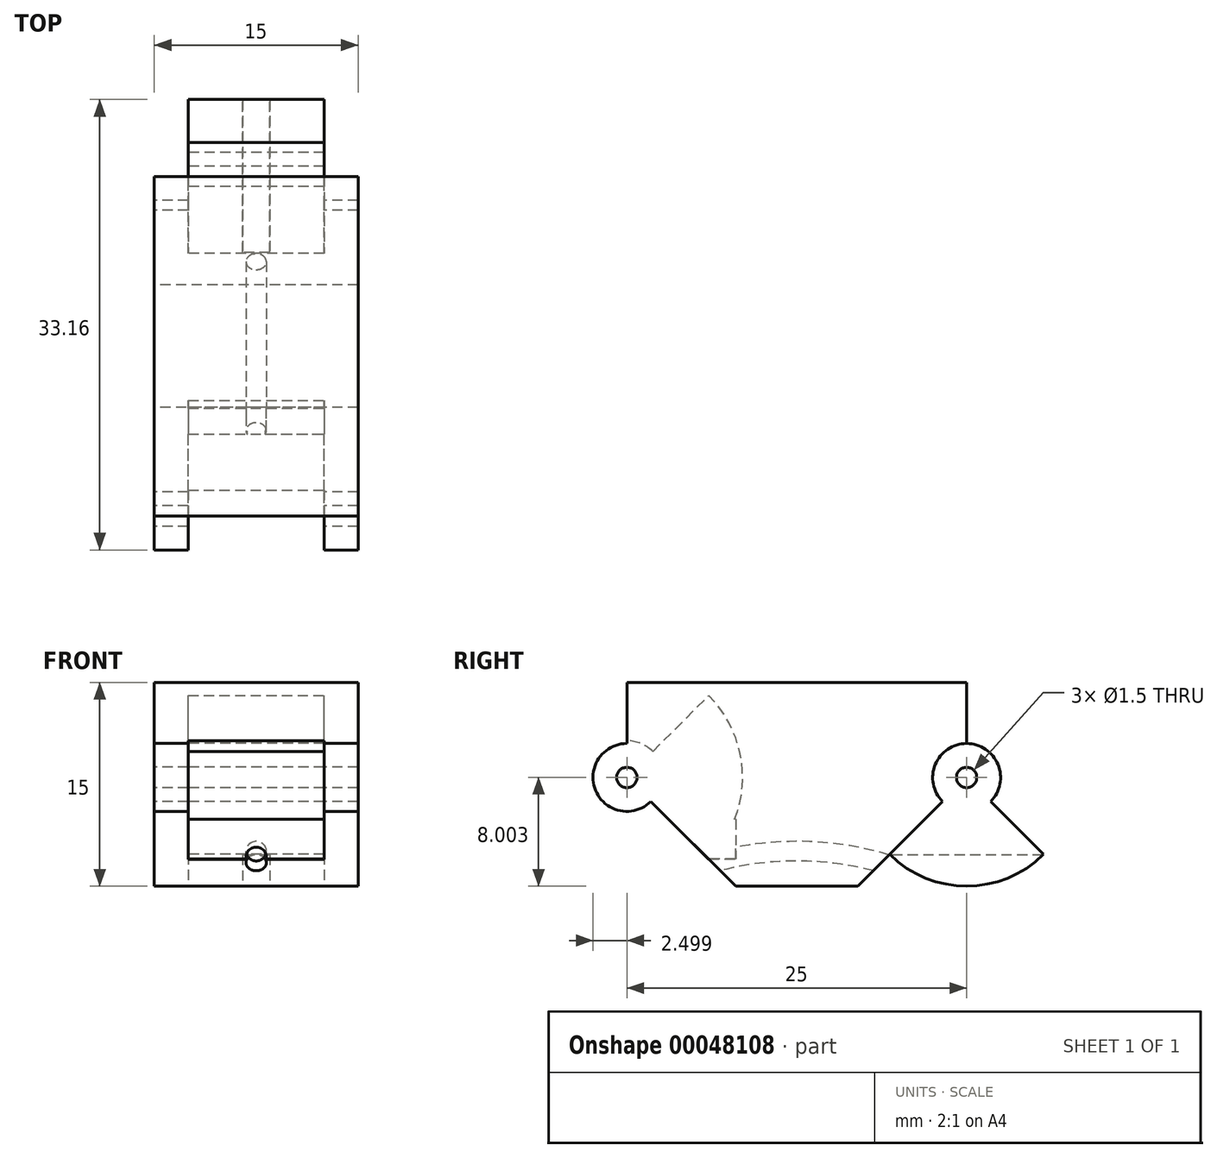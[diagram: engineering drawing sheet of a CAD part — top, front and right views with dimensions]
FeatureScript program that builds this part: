
annotation { "Feature Type Name" : "Feature", "Feature Type Description" : "" }
export const myFeature = defineFeature(function(context is Context, id is Id, definition is map)
    precondition{}
    {
        {
            var Q0;
            Q0=qCreatedBy(makeId("Right.planeOp"),FACE);
            var sketch = newSketch(context, id + "F0", { "sketchPlane" : qUnion([Q0])});
            skLineSegment(sketch, "E0.bottom", {"start": v(-39.16, 7.74) * mm, "end": v(-14.16, 7.74) * mm});
            skLineSegment(sketch, "E0.top", {"start": v(-39.16, -7.26) * mm, "end": v(-14.16, -7.26) * mm});
            skLineSegment(sketch, "E0.left", {"start": v(-39.16, 7.74) * mm, "end": v(-39.16, -7.26) * mm});
            skLineSegment(sketch, "E0.right", {"start": v(-14.16, 7.74) * mm, "end": v(-14.16, -7.26) * mm});
            skCircle(sketch, "E1", {"center": v(-14.16, 0.74) * mm, "radius": 2.5 * mm});
            skCircle(sketch, "E2", {"center": v(-14.16, 0.74) * mm, "radius": 8 * mm});
            skLineSegment(sketch, "E3", {"start": v(-14.16, 0.74) * mm, "end": v(-8.5, -4.91) * mm});
            skCircle(sketch, "E4", {"center": v(-14.16, 0.74) * mm, "radius": 0.75 * mm});
            skLineSegment(sketch, "E5", {"start": v(-14.16, 0.74) * mm, "end": v(-22.16, -7.26) * mm});
            skCircle(sketch, "E6", {"center": v(-39.16, 0.74) * mm, "radius": 2.5 * mm});
            skCircle(sketch, "E7", {"center": v(-39.16, 0.74) * mm, "radius": 0.75 * mm});
            skLineSegment(sketch, "E8", {"start": v(-39.16, 0.74) * mm, "end": v(-31.16, -7.26) * mm});
            skArc(sketch, "E9", {"start": v(-33.14, -5.28) * mm, "mid": v(-30.65, 0.74) * mm, "end": v(-33.14, 6.76) * mm});
            skLineSegment(sketch, "E10", {"start": v(-39.16, 0.74) * mm, "end": v(-32.16, 7.74) * mm});
            skSolve(sketch);
        }
        {
            var Q0;
            {var subQ3=sQuery(id+"F0.wireOp",EDGE,"E0.right");var subQ7=sQuery(id+"F0.wireOp",EDGE,"E0.bottom");var subQ8=makeQuery(id+"F0.imprint","INTERSECT",VERTEX,{"derivedFrom":[subQ7,subQ3]});Q0=makeQuery(id+"F0.imprint","IMPRINT",FACE,{"disambiguationData":[TD([[makeQuery(id+"F0.imprint","IMPRINT",EDGE,{"disambiguationData":[TD([[subQ8,1.0]])],"derivedFrom":subQ7}),-1.0]])]});}
            var Q1;
            {var subQ5=sQuery(id+"F0.wireOp",EDGE,"E0.left");var subQ11=sQuery(id+"F0.wireOp",EDGE,"E0.bottom");var subQ13=makeQuery(id+"F0.imprint","INTERSECT",VERTEX,{"derivedFrom":[subQ11,subQ5]});Q1=makeQuery(id+"F0.imprint","IMPRINT",FACE,{"disambiguationData":[TD([[makeQuery(id+"F0.imprint","IMPRINT",EDGE,{"disambiguationData":[TD([[subQ13,-1.0]])],"derivedFrom":subQ11}),-1.0]])]});}
            var Q2;
            {var subQ3=sQuery(id+"F0.wireOp",EDGE,"E6");var subQ5=sQuery(id+"F0.wireOp",EDGE,"E0.left");var subQ6=makeQuery(id+"F0.imprint","INTERSECT",VERTEX,{"disambiguationData":[OD(1.0)],"derivedFrom":[subQ5,subQ3]});Q2=makeQuery(id+"F0.imprint","IMPRINT",FACE,{"disambiguationData":[TD([[makeQuery(id+"F0.imprint","IMPRINT",EDGE,{"disambiguationData":[TD([[subQ6,1.0]])],"derivedFrom":subQ5}),1.0]])]});}
            var Q3;
            {var subQ1=sQuery(id+"F0.wireOp",EDGE,"E0.left");var subQ4=sQuery(id+"F0.wireOp",EDGE,"E6");var subQ6=makeQuery(id+"F0.imprint","INTERSECT",VERTEX,{"disambiguationData":[OD(0.0)],"derivedFrom":[subQ1,subQ4]});Q3=makeQuery(id+"F0.imprint","IMPRINT",FACE,{"disambiguationData":[TD([[makeQuery(id+"F0.imprint","IMPRINT",EDGE,{"disambiguationData":[TD([[subQ6,-1.0]])],"derivedFrom":subQ1}),-1.0]])]});}
            var Q4;
            {var subQ3=sQuery(id+"F0.wireOp",EDGE,"E6");var subQ5=sQuery(id+"F0.wireOp",EDGE,"E0.left");var subQ7=makeQuery(id+"F0.imprint","INTERSECT",VERTEX,{"disambiguationData":[OD(0.0)],"derivedFrom":[subQ5,subQ3]});Q4=makeQuery(id+"F0.imprint","IMPRINT",FACE,{"disambiguationData":[TD([[makeQuery(id+"F0.imprint","IMPRINT",EDGE,{"disambiguationData":[TD([[subQ7,-1.0]])],"derivedFrom":subQ5}),1.0]])]});}
            var Q5;
            {var subQ0=sQuery(id+"F0.wireOp",EDGE,"E9");Q5=makeQuery(id+"F0.imprint","IMPRINT",FACE,{"disambiguationData":[TD([[makeQuery(id+"F0.imprint","IMPRINT",EDGE,{"derivedFrom":subQ0}),-1.0]])]});}
            var Q6;
            {var subQ3=sQuery(id+"F0.wireOp",EDGE,"E9");Q6=makeQuery(id+"F0.imprint","IMPRINT",FACE,{"disambiguationData":[TD([[makeQuery(id+"F0.imprint","IMPRINT",EDGE,{"derivedFrom":subQ3}),1.0]])]});}
            var Q7;
            {var subQ0=sQuery(id+"F0.wireOp",EDGE,"E10");var subQ3=sQuery(id+"F0.wireOp",EDGE,"E6");var subQ4=makeQuery(id+"F0.imprint","INTERSECT",VERTEX,{"derivedFrom":[subQ3,subQ0]});Q7=makeQuery(id+"F0.imprint","IMPRINT",FACE,{"disambiguationData":[TD([[makeQuery(id+"F0.imprint","IMPRINT",EDGE,{"disambiguationData":[TD([[subQ4,1.0]])],"derivedFrom":subQ3}),1.0]])]});}
            extrude(context, id + "F1", {"entities" : qUnion([Q0, Q1, Q2, Q3, Q4, Q5, Q6, Q7]), "depth" : 15 * mm, "symmetric" : true});
        }
        {
            var Q0;
            {var subQ3=sQuery(id+"F0.wireOp",EDGE,"E1");var subQ5=sQuery(id+"F0.wireOp",EDGE,"E0.right");var subQ6=makeQuery(id+"F0.imprint","INTERSECT",VERTEX,{"disambiguationData":[OD(0.0)],"derivedFrom":[subQ5,subQ3]});Q0=makeQuery(id+"F0.imprint","IMPRINT",FACE,{"disambiguationData":[TD([[makeQuery(id+"F0.imprint","IMPRINT",EDGE,{"disambiguationData":[TD([[subQ6,-1.0]])],"derivedFrom":subQ5}),-1.0]])]});}
            var Q1;
            {var subQ3=sQuery(id+"F0.wireOp",EDGE,"E0.right");var subQ5=sQuery(id+"F0.wireOp",EDGE,"E1");var subQ7=makeQuery(id+"F0.imprint","INTERSECT",VERTEX,{"disambiguationData":[OD(0.0)],"derivedFrom":[subQ3,subQ5]});Q1=makeQuery(id+"F0.imprint","IMPRINT",FACE,{"disambiguationData":[TD([[makeQuery(id+"F0.imprint","IMPRINT",EDGE,{"disambiguationData":[TD([[subQ7,-1.0]])],"derivedFrom":subQ3}),1.0]])]});}
            var Q2;
            {var subQ1=sQuery(id+"F0.wireOp",EDGE,"E4");var subQ5=sQuery(id+"F0.wireOp",EDGE,"E0.right");var subQ7=makeQuery(id+"F0.imprint","INTERSECT",VERTEX,{"disambiguationData":[OD(1.0)],"derivedFrom":[subQ5,subQ1]});Q2=makeQuery(id+"F0.imprint","IMPRINT",FACE,{"disambiguationData":[TD([[makeQuery(id+"F0.imprint","IMPRINT",EDGE,{"disambiguationData":[TD([[subQ7,-1.0]])],"derivedFrom":subQ5}),1.0]])]});}
            var Q3;
            {var subQ0=sQuery(id+"F0.wireOp",EDGE,"E4");var subQ3=sQuery(id+"F0.wireOp",EDGE,"E0.right");var subQ4=makeQuery(id+"F0.imprint","INTERSECT",VERTEX,{"disambiguationData":[OD(1.0)],"derivedFrom":[subQ3,subQ0]});Q3=makeQuery(id+"F0.imprint","IMPRINT",FACE,{"disambiguationData":[TD([[makeQuery(id+"F0.imprint","IMPRINT",EDGE,{"disambiguationData":[TD([[subQ4,-1.0]])],"derivedFrom":subQ3}),-1.0]])]});}
            var Q4;
            {var subQ3=sQuery(id+"F0.wireOp",EDGE,"E0.right");var subQ5=sQuery(id+"F0.wireOp",EDGE,"E1");var subQ7=makeQuery(id+"F0.imprint","INTERSECT",VERTEX,{"disambiguationData":[OD(1.0)],"derivedFrom":[subQ3,subQ5]});Q4=makeQuery(id+"F0.imprint","IMPRINT",FACE,{"disambiguationData":[TD([[makeQuery(id+"F0.imprint","IMPRINT",EDGE,{"disambiguationData":[TD([[subQ7,1.0]])],"derivedFrom":subQ5}),-1.0]])]});}
            var Q5;
            {var subQ1=sQuery(id+"F0.wireOp",EDGE,"E1");var subQ5=sQuery(id+"F0.wireOp",EDGE,"E0.right");var subQ7=makeQuery(id+"F0.imprint","INTERSECT",VERTEX,{"disambiguationData":[OD(1.0)],"derivedFrom":[subQ5,subQ1]});Q5=makeQuery(id+"F0.imprint","IMPRINT",FACE,{"disambiguationData":[TD([[makeQuery(id+"F0.imprint","IMPRINT",EDGE,{"disambiguationData":[TD([[subQ7,-1.0]])],"derivedFrom":subQ1}),-1.0]])]});}
            extrude(context, id + "F2", {"entities" : qUnion([Q0, Q1, Q2, Q3, Q4, Q5]), "operationType" : NewBodyOperationType.ADD, "depth" : 10 * mm, "symmetric" : true});
        }
        {
            var Q0;
            Q0=qCreatedBy(makeId("Right.planeOp"),FACE);
            var sketch = newSketch(context, id + "F3", { "sketchPlane" : qUnion([Q0])});
            skCircle(sketch, "E11", {"center": v(-39.16, 0.74) * mm, "radius": 2.7 * mm});
            skSolve(sketch);
        }
        {
            var Q0;
            Q0 = qSketchRegion(id + "F3", true);
            extrude(context, id + "F4", {"entities" : qUnion([Q0]), "operationType" : NewBodyOperationType.REMOVE, "oppositeDirection" : true, "depth" : 10 * mm, "symmetric" : true});
        }
        {
            var Q0;
            {var subQ0=sQuery(id+"F0.wireOp",EDGE,"E0.left");Q0=makeQuery(id+"F1.opExtrude","SWEPT_FACE",FACE,{"disambiguationData":[OSD([subQ0]),TDD([makeQuery(id+"F0.imprint","IMPRINT",EDGE,{"disambiguationData":[TD([[makeQuery(id+"F0.imprint","INTERSECT",VERTEX,{"derivedFrom":[sQuery(id+"F0.wireOp",EDGE,"E0.bottom"),subQ0]}),-1.0]])],"derivedFrom":subQ0})])]});}
            var sketch = newSketch(context, id + "F5", { "sketchPlane" : qUnion([Q0])});
            skLineSegment(sketch, "E12.bottom", {"start": v(5, -2.35) * mm, "end": v(-5, -2.35) * mm});
            skLineSegment(sketch, "E12.top", {"start": v(5, -5.26) * mm, "end": v(-5, -5.26) * mm});
            skLineSegment(sketch, "E12.left", {"start": v(5, -2.35) * mm, "end": v(5, -5.26) * mm});
            skLineSegment(sketch, "E12.right", {"start": v(-5, -2.35) * mm, "end": v(-5, -5.26) * mm});
            skSolve(sketch);
        }
        {
            var Q0;
            Q0 = qSketchRegion(id + "F5", true);
            extrude(context, id + "F6", {"entities" : qUnion([Q0]), "operationType" : NewBodyOperationType.REMOVE, "oppositeDirection" : true, "depth" : 8 * mm});
        }
        {
            var Q0;
            {var subQ3=sQuery(id+"F0.wireOp",EDGE,"E9");Q0=makeQuery(id+"F0.imprint","IMPRINT",FACE,{"disambiguationData":[TD([[makeQuery(id+"F0.imprint","IMPRINT",EDGE,{"derivedFrom":subQ3}),1.0]])]});}
            extrude(context, id + "F7", {"entities" : qUnion([Q0]), "operationType" : NewBodyOperationType.REMOVE, "oppositeDirection" : true, "depth" : 10 * mm, "symmetric" : true});
        }
        {
            var Q0;
            Q0=makeQuery(id+"F1.opExtrude","SWEPT_FACE",FACE,{"disambiguationData":[OSD([sQuery(id+"F0.wireOp",EDGE,"E0.top")])]});
            var sketch = newSketch(context, id + "F8", { "sketchPlane" : qUnion([Q0])});
            skLineSegment(sketch, "E13.rect.bottom", {"start": v(-1, 8.47) * mm, "end": v(1, 8.47) * mm});
            skLineSegment(sketch, "E13.rect.top", {"start": v(-1, 19.85) * mm, "end": v(1, 19.85) * mm});
            skLineSegment(sketch, "E13.rect.left", {"start": v(-1, 8.47) * mm, "end": v(-1, 19.85) * mm});
            skLineSegment(sketch, "E13.rect.right", {"start": v(1, 8.47) * mm, "end": v(1, 19.85) * mm});
            skPoint(sketch, "E13.rect.middle", {"position": v(0, 14.16) * mm});
            skSolve(sketch);
        }
        {
            var Q0;
            Q0 = qSketchRegion(id + "F8", true);
            extrude(context, id + "F9", {"entities" : qUnion([Q0]), "operationType" : NewBodyOperationType.REMOVE, "oppositeDirection" : true, "depth" : 2.3 * mm});
        }
        {
            var Q0;
            Q0=makeQuery(id+"F1.opExtrude","SWEPT_FACE",FACE,{"disambiguationData":[OSD([sQuery(id+"F0.wireOp",EDGE,"E0.left")])]});
            cPlane(context, id + "F10", {"entities" : qUnion([Q0]), "cplaneType" : CPlaneType.OFFSET, "offset" : 6.02 * mm, "oppositeDirection" : true, "width" : 150 * mm, "height" : 150 * mm});
        }
        {
            var Q0;
            Q0=qCreatedBy(id+"F10.planeOp",FACE);
            var sketch = newSketch(context, id + "F11", { "sketchPlane" : qUnion([Q0])});
            skCircle(sketch, "E14", {"center": v(0, -5.61) * mm, "radius": 0.75 * mm});
            skSolve(sketch);
        }
        {
            var Q0;
            Q0=qCreatedBy(makeId("Right.planeOp"),FACE);
            var sketch = newSketch(context, id + "F12", { "sketchPlane" : qUnion([Q0])});
            skArc(sketch, "E15", {"start": v(-20.2, -5.61) * mm, "mid": v(-26.67, -4.68) * mm, "end": v(-33.14, -5.61) * mm});
            skSolve(sketch);
        }
        {
            var Q0;
            Q0 = qSketchRegion(id + "F11", true);
            var Q1;
            Q1 = qConstructionFilter(qBodyType(qCreatedBy(id + "F12" ,EDGE), BodyType.WIRE), ConstructionObject.NO);
            sweep(context, id + "F13", {"operationType" : NewBodyOperationType.REMOVE, "profiles" : qUnion([Q0]), "path" : qUnion([Q1])});
        }
    });
